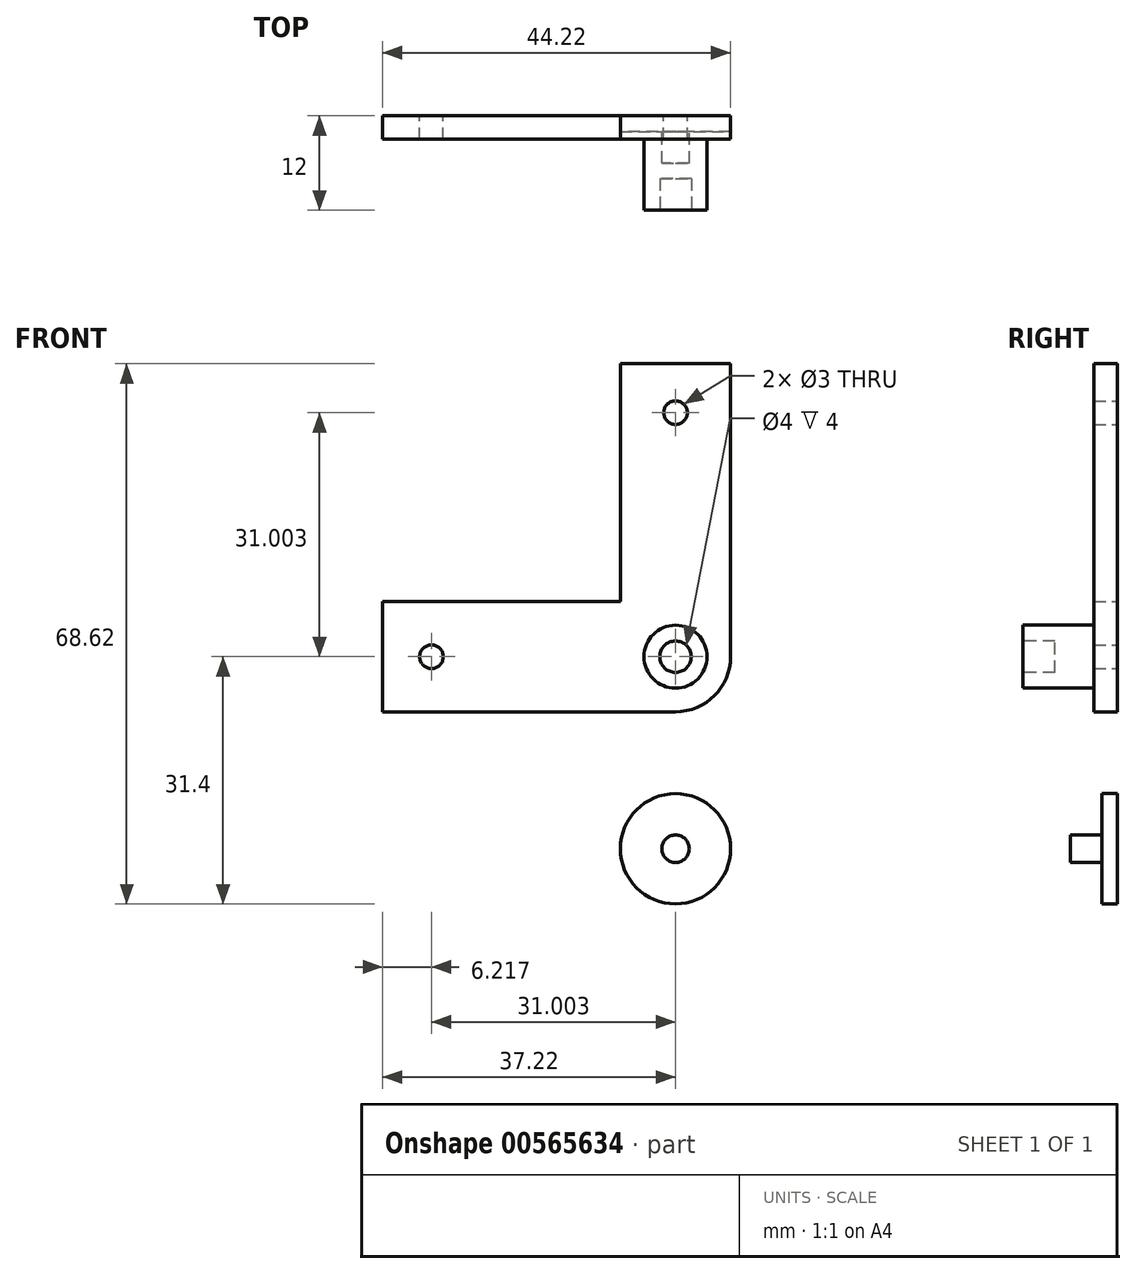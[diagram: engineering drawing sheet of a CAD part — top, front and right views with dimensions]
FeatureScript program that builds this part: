
annotation { "Feature Type Name" : "Feature", "Feature Type Description" : "" }
export const myFeature = defineFeature(function(context is Context, id is Id, definition is map)
    precondition{}
    {
        {
            var Q0;
            Q0=qCreatedBy(makeId("Front.planeOp"),FACE);
            var sketch = newSketch(context, id + "F0", { "sketchPlane" : qUnion([Q0])});
            skArc(sketch, "E0", {"start": v(0, -7) * mm, "mid": v(4.95, -4.95) * mm, "end": v(7, 0) * mm});
            skLineSegment(sketch, "E1", {"start": v(-7, 7) * mm, "end": v(-7, 37.22) * mm});
            skLineSegment(sketch, "E2", {"start": v(7, 0) * mm, "end": v(7, 37.22) * mm});
            skLineSegment(sketch, "E3", {"start": v(-7, 7) * mm, "end": v(-37.22, 7) * mm});
            skLineSegment(sketch, "E4", {"start": v(0, -7) * mm, "end": v(-37.22, -7) * mm});
            skLineSegment(sketch, "E5", {"start": v(-37.22, 7) * mm, "end": v(-37.22, -7) * mm});
            skLineSegment(sketch, "E6", {"start": v(-7, 37.22) * mm, "end": v(7, 37.22) * mm});
            skCircle(sketch, "E7", {"center": v(0, 0) * mm, "radius": 4 * mm});
            skLineSegment(sketch, "E8", {"start": v(-31, 7) * mm, "end": v(-31, -7) * mm, "construction": true});
            skLineSegment(sketch, "E9", {"start": v(-37.22, 0) * mm, "end": v(-31, 0) * mm, "construction": true});
            skLineSegment(sketch, "E10", {"start": v(-7, 31) * mm, "end": v(7, 31) * mm, "construction": true});
            skLineSegment(sketch, "E11", {"start": v(0, 37.22) * mm, "end": v(0, 31) * mm, "construction": true});
            skCircle(sketch, "E12", {"center": v(-31, 0) * mm, "radius": 1.5 * mm});
            skCircle(sketch, "E13", {"center": v(0, 31) * mm, "radius": 1.5 * mm});
            skSolve(sketch);
        }
        {
            var Q0;
            Q0=makeQuery(id+"F0.imprint","IMPRINT",FACE,{"disambiguationData":[TD([[makeQuery(id+"F0.imprint","IMPRINT",EDGE,{"derivedFrom":sQuery(id+"F0.wireOp",EDGE,"E0")}),1.0]])]});
            extrude(context, id + "F1", {"entities" : qUnion([Q0]), "depth" : 3 * mm, "offsetDistance" : 25 * mm});
        }
        {
            var Q0;
            Q0=makeQuery(id+"F0.imprint","IMPRINT",FACE,{"disambiguationData":[TD([[makeQuery(id+"F0.imprint","IMPRINT",EDGE,{"derivedFrom":sQuery(id+"F0.wireOp",EDGE,"E7")}),1.0]])]});
            extrude(context, id + "F2", {"entities" : qUnion([Q0]), "operationType" : NewBodyOperationType.ADD, "depth" : 12 * mm, "offsetDistance" : 25 * mm});
        }
        {
            var Q0;
            Q0=makeQuery(id+"F2.opExtrude","CAP_FACE",FACE,{"disambiguationData":[OSD([sQuery(id+"F0.wireOp",EDGE,"E7")])],"isStart":false});
            var sketch = newSketch(context, id + "F3", { "sketchPlane" : qUnion([Q0])});
            skPoint(sketch, "E14", {"position": v(0, 0) * mm});
            skCircle(sketch, "E15", {"center": v(0, 0) * mm, "radius": 2 * mm});
            skSolve(sketch);
        }
        {
            var Q0;
            Q0=qCreatedBy(makeId("Front.planeOp"),FACE);
            var sketch = newSketch(context, id + "F4", { "sketchPlane" : qUnion([Q0])});
            skCircle(sketch, "E16", {"center": v(0, -24.4) * mm, "radius": 7 * mm});
            skCircle(sketch, "E17", {"center": v(0, -24.4) * mm, "radius": 1.75 * mm});
            skSolve(sketch);
        }
        {
            var Q0;
            Q0=makeQuery(id+"F4.imprint","IMPRINT",FACE,{"disambiguationData":[TD([[makeQuery(id+"F4.imprint","IMPRINT",EDGE,{"derivedFrom":sQuery(id+"F4.wireOp",EDGE,"E16")}),1.0]])]});
            extrude(context, id + "F5", {"entities" : qUnion([Q0]), "depth" : 2 * mm, "offsetDistance" : 25 * mm});
        }
        {
            var Q0;
            Q0=makeQuery(id+"F4.imprint","IMPRINT",FACE,{"disambiguationData":[TD([[makeQuery(id+"F4.imprint","IMPRINT",EDGE,{"derivedFrom":sQuery(id+"F4.wireOp",EDGE,"E17")}),1.0]])]});
            extrude(context, id + "F6", {"entities" : qUnion([Q0]), "operationType" : NewBodyOperationType.ADD, "depth" : 6 * mm, "offsetDistance" : 25 * mm});
        }
        {
            var Q0;
            Q0=makeQuery(id+"F3.imprint","IMPRINT",FACE,{"disambiguationData":[TD([[makeQuery(id+"F3.imprint","IMPRINT",EDGE,{"derivedFrom":sQuery(id+"F3.wireOp",EDGE,"E15")}),1.0]])]});
            extrude(context, id + "F7", {"entities" : qUnion([Q0]), "operationType" : NewBodyOperationType.REMOVE, "oppositeDirection" : true, "depth" : 4 * mm, "offsetDistance" : 25 * mm});
        }
    });
